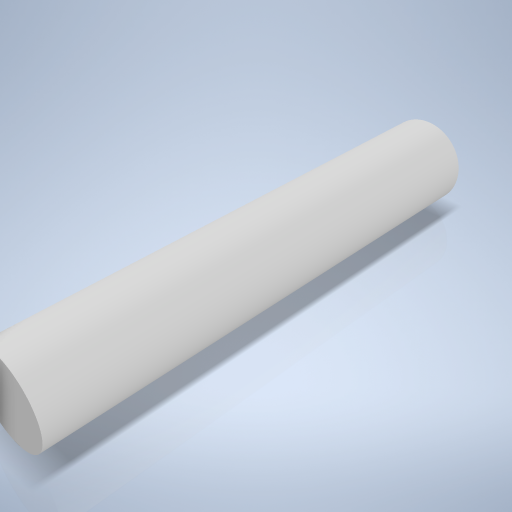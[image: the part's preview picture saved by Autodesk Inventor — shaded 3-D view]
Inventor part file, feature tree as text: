
AUTODESK INVENTOR PART (.ipt)
format: ipt  version: 2024.2 (Build 282272000, 272)  size: 231,424 bytes
history: native  units: mm
features: extrude x1, sketch x1
ambient origin geometry x8: Origin, YZ Plane, XZ Plane, XY Plane, X Axis, Y Axis, Z Axis, Center Point
bodies: Volumenkörper1 (feature_tree)
feature tree (2):
  extrude  "Extrusion1"  Depth=56.0mm TaperAngle=0.0deg
  sketch  "Skizze1"  dims[d0=10.0mm d1=56.0mm d2=0.0mm]
